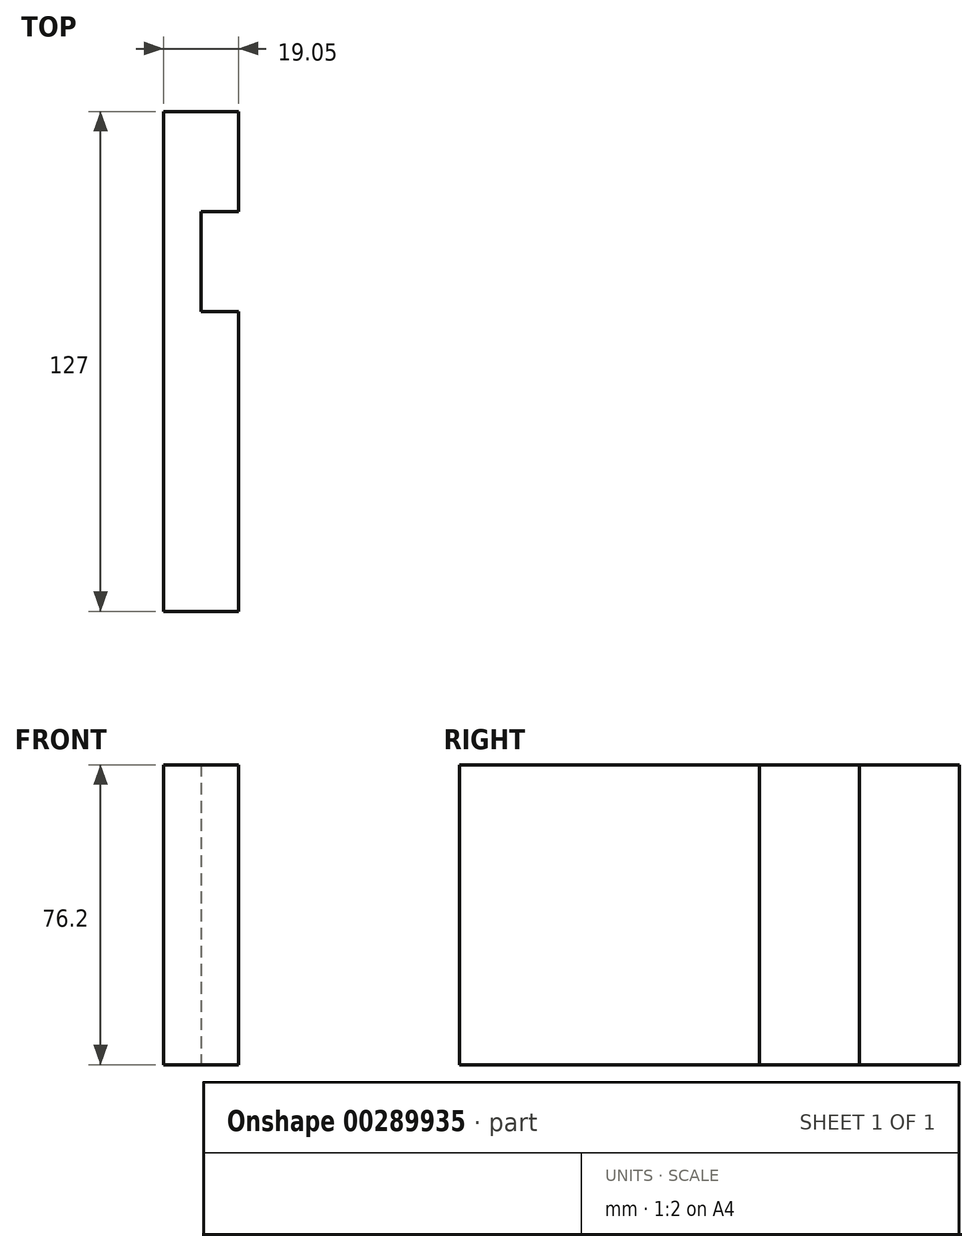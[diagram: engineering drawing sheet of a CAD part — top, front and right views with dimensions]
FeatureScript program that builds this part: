
annotation { "Feature Type Name" : "Feature", "Feature Type Description" : "" }
export const myFeature = defineFeature(function(context is Context, id is Id, definition is map)
    precondition{}
    {
        {
            var Q0;
            Q0=qCreatedBy(makeId("Top.planeOp"),FACE);
            var sketch = newSketch(context, id + "F0", { "sketchPlane" : qUnion([Q0])});
            skLineSegment(sketch, "E0.bottom", {"start": v(-34.04, 123.61) * mm, "end": v(-14.99, 123.61) * mm});
            skLineSegment(sketch, "E0.top", {"start": v(-34.04, -3.39) * mm, "end": v(-14.99, -3.39) * mm});
            skLineSegment(sketch, "E0.left", {"start": v(-34.04, 123.61) * mm, "end": v(-34.04, -3.39) * mm});
            skLineSegment(sketch, "E0.right", {"start": v(-14.99, 123.61) * mm, "end": v(-14.99, 98.21) * mm});
            skLineSegment(sketch, "E1", {"start": v(-14.99, 98.21) * mm, "end": v(-24.51, 98.21) * mm});
            skLineSegment(sketch, "E2", {"start": v(-24.51, 98.21) * mm, "end": v(-24.51, 72.81) * mm});
            skLineSegment(sketch, "E3", {"start": v(-24.51, 72.81) * mm, "end": v(-14.99, 72.81) * mm});
            skLineSegment(sketch, "E4.trimOffspring", {"start": v(-14.99, 72.81) * mm, "end": v(-14.99, -3.39) * mm});
            skSolve(sketch);
        }
        {
            var Q0;
            Q0 = qSketchRegion(id + "F0", true);
            extrude(context, id + "F1", {"entities" : qUnion([Q0]), "depth" : 76.2 * mm});
        }
    });
